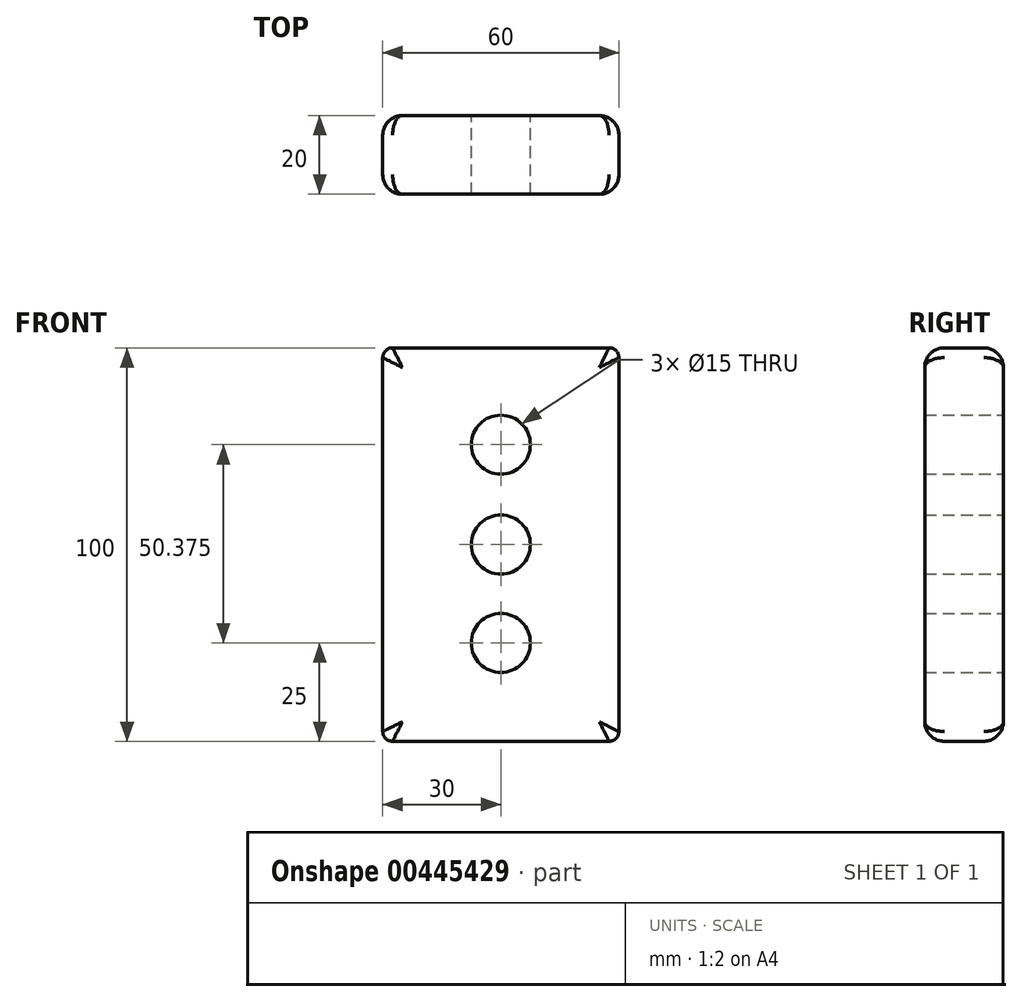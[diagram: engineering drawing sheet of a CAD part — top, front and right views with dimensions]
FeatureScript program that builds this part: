
annotation { "Feature Type Name" : "Feature", "Feature Type Description" : "" }
export const myFeature = defineFeature(function(context is Context, id is Id, definition is map)
    precondition{}
    {
        {
            var Q0;
            Q0=qCreatedBy(makeId("Front.planeOp"),FACE);
            var sketch = newSketch(context, id + "F0", { "sketchPlane" : qUnion([Q0])});
            skLineSegment(sketch, "E0.bottom", {"start": v(-30, 50) * mm, "end": v(30, 50) * mm});
            skLineSegment(sketch, "E0.top", {"start": v(-30, -50) * mm, "end": v(30, -50) * mm});
            skLineSegment(sketch, "E0.left", {"start": v(-30, 50) * mm, "end": v(-30, -50) * mm});
            skLineSegment(sketch, "E0.right", {"start": v(30, 50) * mm, "end": v(30, -50) * mm});
            skPoint(sketch, "E0.middle", {"position": v(0, 0) * mm});
            skCircle(sketch, "E1", {"center": v(0, 0) * mm, "radius": 7.5 * mm});
            skLineSegment(sketch, "E2", {"start": v(0, 7.5) * mm, "end": v(0, 17.5) * mm});
            skCircle(sketch, "E3", {"center": v(0, 25.37) * mm, "radius": 7.5 * mm});
            skLineSegment(sketch, "E4", {"start": v(0, -7.5) * mm, "end": v(0, -17.5) * mm});
            skCircle(sketch, "E5", {"center": v(0, -25) * mm, "radius": 7.5 * mm});
            skSolve(sketch);
        }
        {
            var Q0;
            Q0=makeQuery(id+"F0.imprint","IMPRINT",FACE,{"disambiguationData":[TD([[makeQuery(id+"F0.imprint","IMPRINT",EDGE,{"derivedFrom":sQuery(id+"F0.wireOp",EDGE,"E0.bottom")}),-1.0]])]});
            extrude(context, id + "F1", {"entities" : qUnion([Q0]), "depth" : 20 * mm});
        }
        {
            var Q0;
            Q0=makeQuery(id+"F1.opExtrude","SWEPT_EDGE",EDGE,{"disambiguationData":[OSD([sQuery(id+"F0.wireOp",EDGE,"E0.bottom"),sQuery(id+"F0.wireOp",EDGE,"E0.right")])]});
            var Q1;
            Q1=makeQuery(id+"F1.opExtrude","SWEPT_EDGE",EDGE,{"disambiguationData":[OSD([sQuery(id+"F0.wireOp",EDGE,"E0.bottom"),sQuery(id+"F0.wireOp",EDGE,"E0.left")])]});
            var Q2;
            Q2=makeQuery(id+"F1.opExtrude","SWEPT_EDGE",EDGE,{"disambiguationData":[OSD([sQuery(id+"F0.wireOp",EDGE,"E0.top"),sQuery(id+"F0.wireOp",EDGE,"E0.right")])]});
            var Q3;
            Q3=makeQuery(id+"F1.opExtrude","SWEPT_EDGE",EDGE,{"disambiguationData":[OSD([sQuery(id+"F0.wireOp",EDGE,"E0.top"),sQuery(id+"F0.wireOp",EDGE,"E0.left")])]});
            fillet(context, id + "F2", {"entities" : qUnion([Q0, Q1, Q2, Q3]), "radius" : 2.5 * mm, "tangentPropagation" : true, "allowEdgeOverflow" : false});
        }
        {
            var Q0;
            Q0=makeQuery(id+"F1.opExtrude","CAP_EDGE",EDGE,{"disambiguationData":[OSD([sQuery(id+"F0.wireOp",EDGE,"E0.bottom")])],"isStart":true});
            var Q1;
            Q1=makeQuery(id+"F1.opExtrude","CAP_EDGE",EDGE,{"disambiguationData":[OSD([sQuery(id+"F0.wireOp",EDGE,"E0.top")])],"isStart":false});
            fillet(context, id + "F3", {"entities" : qUnion([Q0, Q1]), "radius" : 5 * mm, "tangentPropagation" : true, "allowEdgeOverflow" : false});
        }
    });
